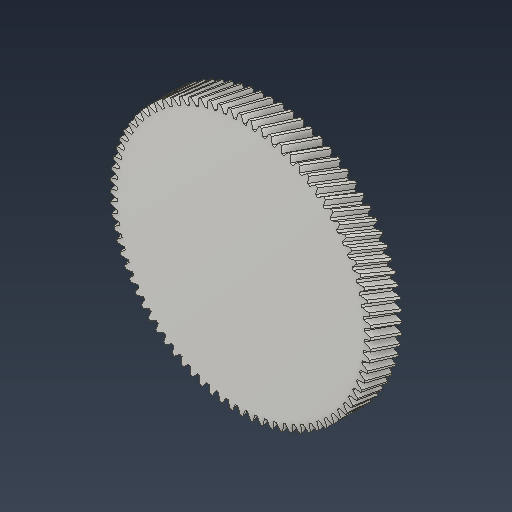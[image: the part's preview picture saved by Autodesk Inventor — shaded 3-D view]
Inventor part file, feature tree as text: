
AUTODESK INVENTOR PART (.ipt)
format: ipt  version: 2022 (Build 260153000, 153)  size: 1,012,224 bytes
history: native  units: mm (DEFAULTED — no unit token found)
features: plane x3, other x3, sketch x2, extrude x1
ambient origin geometry x8: Origin, YZ Plane, XZ Plane, XY Plane, X Axis, Y Axis, Z Axis, Center Point
bodies: Solid1 (feature_tree)
feature tree (9):
  extrude  "Extrusion1"  Depth=20.0mm TaperAngle=0.0deg
  plane  "Work Plane2"
  plane  "Work Plane8"
  plane  "Work Plane9"
  other  "Spur Gear"
  sketch  "Sketch1"  dims[d0=169.432889mm d1=20.0mm d2=0.0mm]
  sketch  "Sketch2"  dims[d3=170.268444mm d4=10.0mm d5=0.0mm d16=104.0mm d17=0.0mm d34=0.392699mm d39=0.0mm d41=0.0mm d43=104.0mm d46=104.0mm d47=0.0mm d48=0.0mm]
  other  "Srf1"
  other  "Pitch Diameter"
